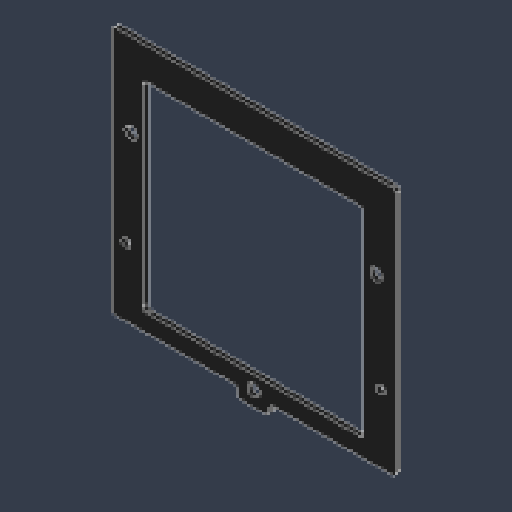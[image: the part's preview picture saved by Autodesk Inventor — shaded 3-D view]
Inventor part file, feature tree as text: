
AUTODESK INVENTOR PART (.ipt)
format: ipt  version: 2023.4 (Build 274418000, 418)  size: 274,432 bytes
history: native  units: mm
features: sketch x9, extrude x8, hole x1, fillet x1, projected_geometry x1
ambient origin geometry x8: Origin, YZ Plane, XZ Plane, XY Plane, X Axis, Y Axis, Z Axis, Center Point
bodies: Solid1 (feature_tree)
feature tree (20):
  extrude  "Extrusion1"  Depth=65.0mm
  hole  "Hole1"  [1 undecoded]
  extrude  "Extrusion2"  Depth=9.0mm
  extrude  "Extrusion3"  TaperAngle=45.0deg  [1 undecoded]
  extrude  "Extrusion4"  Depth=8.0mm
  extrude  "Extrusion5"  Depth=4.0mm
  extrude  "Extrusion6"  Depth=71.4mm
  extrude  "Extrusion7"  Depth=1.0mm
  fillet  "Fillet1"  Radius=9.0mm
  extrude  "Extrusion8"  Depth=1.0mm
  sketch  "Sketch1"  dims[d0=80.0mm d1=65.0mm]
  sketch  "Sketch2"  dims[d2=19.0mm d3=45.0deg]
  sketch  "Sketch4"  dims[d4=9.0mm d5=3.5mm]
  sketch  "Sketch5"  dims[d6=6.0mm d7=45.0deg]
  sketch  "Sketch6"  dims[d8=8.0mm d9=8.0mm]
  sketch  "Sketch7"  dims[d10=12.0mm d11=4.0mm]
  sketch  "Sketch8"  dims[d12=1.3mm d13=0.0mm d14=71.4mm]
  sketch  "Sketch9"  dims[d15=22.7mm]
  sketch  "Sketch10"  dims[d16=2.5mm d17=6.0mm d18=40.0mm d19=25.5mm d20=90.0deg d21=8.0mm d22=20.594885mm d23=3.2mm d24=9.0mm d25=0.4mm d26=6.8mm d27=0.0mm d28=3.4mm d29=68.8mm d30=27.4mm d31=18.0mm d32=0.4mm d33=0.0mm d34=0.0mm d35=0.0mm d36=9.0mm d37=9.0mm d38=9.0mm d39=5.0mm d40=10.0mm d41=0.0mm d42=51.0mm d43=8.0mm d44=5.0mm d45=5.0mm d46=0.0mm d47=0.0mm d48=0.0mm d49=0.0mm d50=1.0mm d51=0.1mm d52=0.0mm]
  projected_geometry  "Projected Loop1"
note: 2 required parameter values undecoded (feature->parameter linkage not recoverable at this tier; creation-order binding heuristic only, values carry confidence <= 0.55)
